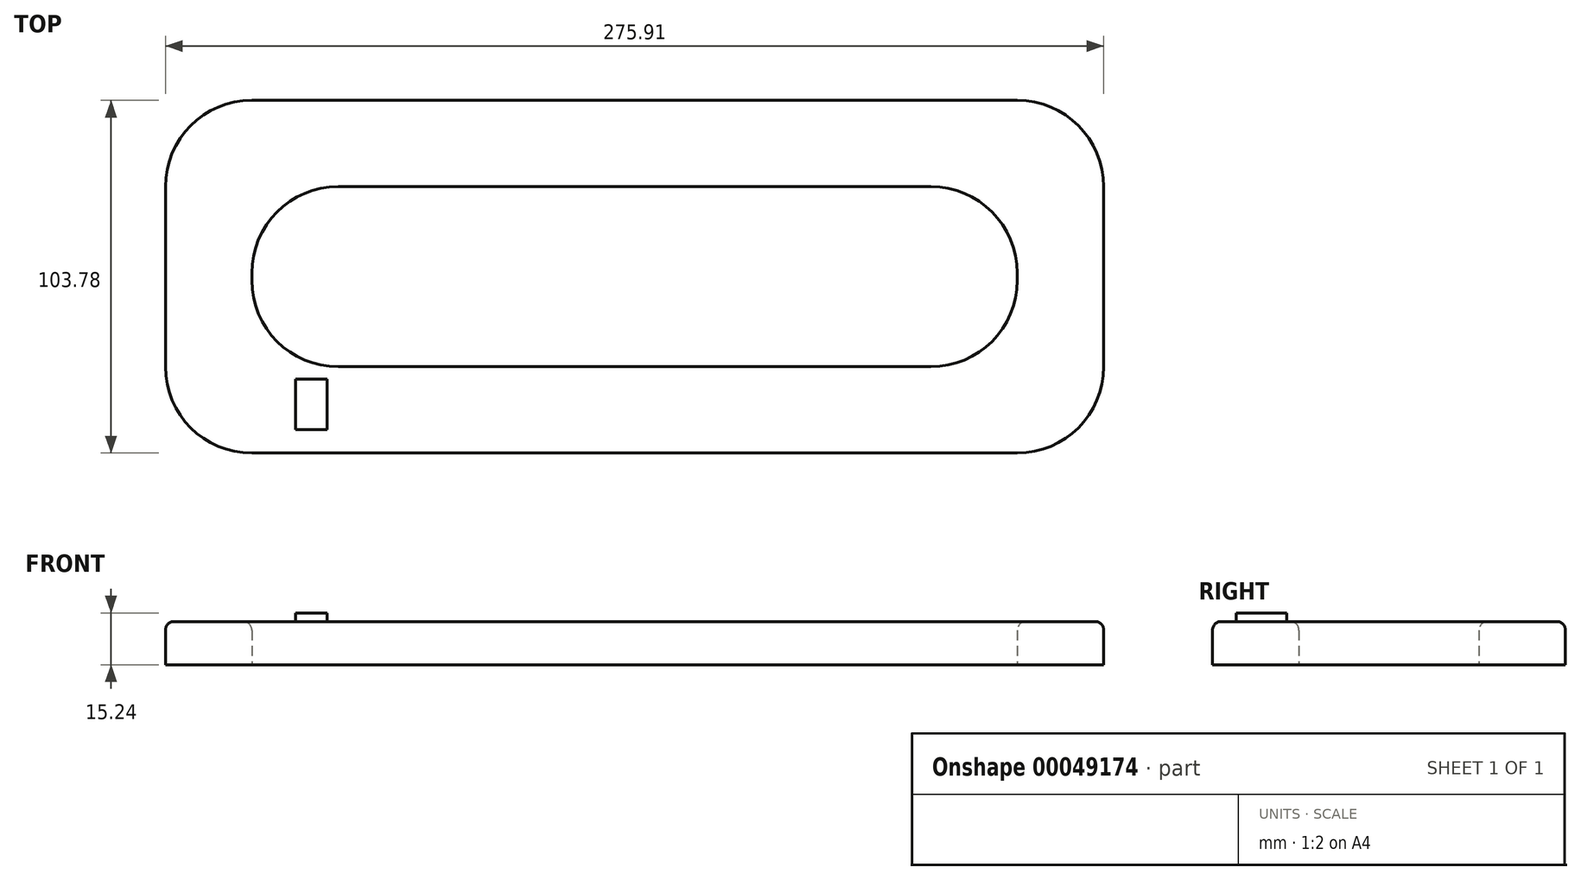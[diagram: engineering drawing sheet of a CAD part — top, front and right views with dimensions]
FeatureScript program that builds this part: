
annotation { "Feature Type Name" : "Feature", "Feature Type Description" : "" }
export const myFeature = defineFeature(function(context is Context, id is Id, definition is map)
    precondition{}
    {
        {
            var Q0;
            Q0=qCreatedBy(makeId("Top.planeOp"),FACE);
            var sketch = newSketch(context, id + "F0", { "sketchPlane" : qUnion([Q0])});
            skLineSegment(sketch, "E0.bottom", {"start": v(-102.88, -42.5) * mm, "end": v(71.43, -42.5) * mm});
            skLineSegment(sketch, "E0.top", {"start": v(-102.88, 10.48) * mm, "end": v(71.43, 10.48) * mm});
            skLineSegment(sketch, "E0.left", {"start": v(-128.28, -17.1) * mm, "end": v(-128.28, -14.92) * mm});
            skLineSegment(sketch, "E0.right", {"start": v(96.83, -17.1) * mm, "end": v(96.83, -14.92) * mm});
            skPoint(sketch, "E1.visualSharp", {"position": v(-128.28, 10.48) * mm});
            skArc(sketch, "E1.filletArc", {"start": v(-102.88, 10.48) * mm, "mid": v(-120.84, 3.04) * mm, "end": v(-128.28, -14.92) * mm});
            skPoint(sketch, "E2.visualSharp", {"position": v(-128.28, -42.5) * mm});
            skArc(sketch, "E2.filletArc", {"start": v(-128.28, -17.1) * mm, "mid": v(-120.84, -35.06) * mm, "end": v(-102.88, -42.5) * mm});
            skPoint(sketch, "E3.visualSharp", {"position": v(96.83, -42.5) * mm});
            skArc(sketch, "E3.filletArc", {"start": v(71.43, -42.5) * mm, "mid": v(89.4, -35.06) * mm, "end": v(96.83, -17.1) * mm});
            skPoint(sketch, "E4.visualSharp", {"position": v(96.83, 10.48) * mm});
            skArc(sketch, "E4.filletArc", {"start": v(96.83, -14.92) * mm, "mid": v(89.4, 3.04) * mm, "end": v(71.43, 10.48) * mm});
            skLineSegment(sketch, "E5.bottom", {"start": v(-128.28, 35.88) * mm, "end": v(96.83, 35.88) * mm});
            skLineSegment(sketch, "E5.top", {"start": v(-128.28, -67.9) * mm, "end": v(96.83, -67.9) * mm});
            skLineSegment(sketch, "E5.left", {"start": v(-153.68, 10.48) * mm, "end": v(-153.68, -42.5) * mm});
            skLineSegment(sketch, "E5.right", {"start": v(122.23, 10.48) * mm, "end": v(122.23, -42.5) * mm});
            skPoint(sketch, "E6.visualSharp", {"position": v(-153.68, -67.9) * mm});
            skArc(sketch, "E6.filletArc", {"start": v(-153.68, -42.5) * mm, "mid": v(-146.24, -60.46) * mm, "end": v(-128.28, -67.9) * mm});
            skPoint(sketch, "E7.visualSharp", {"position": v(-153.68, 35.88) * mm});
            skArc(sketch, "E7.filletArc", {"start": v(-128.28, 35.88) * mm, "mid": v(-146.24, 28.44) * mm, "end": v(-153.68, 10.48) * mm});
            skPoint(sketch, "E8.visualSharp", {"position": v(122.23, 35.88) * mm});
            skArc(sketch, "E8.filletArc", {"start": v(122.23, 10.48) * mm, "mid": v(114.8, 28.44) * mm, "end": v(96.83, 35.88) * mm});
            skPoint(sketch, "E9.visualSharp", {"position": v(122.23, -67.9) * mm});
            skArc(sketch, "E9.filletArc", {"start": v(96.83, -67.9) * mm, "mid": v(114.8, -60.46) * mm, "end": v(122.23, -42.5) * mm});
            skSolve(sketch);
        }
        {
            var Q0;
            Q0=makeQuery(id+"F0.imprint","IMPRINT",FACE,{"disambiguationData":[TD([[makeQuery(id+"F0.imprint","IMPRINT",EDGE,{"derivedFrom":sQuery(id+"F0.wireOp",EDGE,"E0.bottom")}),-1.0]])]});
            extrude(context, id + "F1", {"entities" : qUnion([Q0]), "depth" : 12.7 * mm});
        }
        {
            var Q0;
            Q0=makeQuery(id+"F1.opExtrude","CAP_FACE",FACE,{"disambiguationData":[OSD([sQuery(id+"F0.wireOp",EDGE,"E0.bottom"),sQuery(id+"F0.wireOp",EDGE,"E0.top"),sQuery(id+"F0.wireOp",EDGE,"E0.left"),sQuery(id+"F0.wireOp",EDGE,"E0.right"),sQuery(id+"F0.wireOp",EDGE,"E1.filletArc"),sQuery(id+"F0.wireOp",EDGE,"E2.filletArc"),sQuery(id+"F0.wireOp",EDGE,"E3.filletArc"),sQuery(id+"F0.wireOp",EDGE,"E4.filletArc"),sQuery(id+"F0.wireOp",EDGE,"E5.bottom"),sQuery(id+"F0.wireOp",EDGE,"E5.top"),sQuery(id+"F0.wireOp",EDGE,"E5.left"),sQuery(id+"F0.wireOp",EDGE,"E5.right"),sQuery(id+"F0.wireOp",EDGE,"E6.filletArc"),sQuery(id+"F0.wireOp",EDGE,"E7.filletArc"),sQuery(id+"F0.wireOp",EDGE,"E8.filletArc"),sQuery(id+"F0.wireOp",EDGE,"E9.filletArc")])],"isStart":false});
            fillet(context, id + "F2", {"entities" : qUnion([Q0]), "radius" : 2.54 * mm, "tangentPropagation" : true, "allowEdgeOverflow" : false});
        }
        {
            var Q0;
            Q0=makeQuery(id+"F1.opExtrude","CAP_FACE",FACE,{"disambiguationData":[OSD([sQuery(id+"F0.wireOp",EDGE,"E0.bottom"),sQuery(id+"F0.wireOp",EDGE,"E0.top"),sQuery(id+"F0.wireOp",EDGE,"E0.left"),sQuery(id+"F0.wireOp",EDGE,"E0.right"),sQuery(id+"F0.wireOp",EDGE,"E1.filletArc"),sQuery(id+"F0.wireOp",EDGE,"E2.filletArc"),sQuery(id+"F0.wireOp",EDGE,"E3.filletArc"),sQuery(id+"F0.wireOp",EDGE,"E4.filletArc"),sQuery(id+"F0.wireOp",EDGE,"E5.bottom"),sQuery(id+"F0.wireOp",EDGE,"E5.top"),sQuery(id+"F0.wireOp",EDGE,"E5.left"),sQuery(id+"F0.wireOp",EDGE,"E5.right"),sQuery(id+"F0.wireOp",EDGE,"E6.filletArc"),sQuery(id+"F0.wireOp",EDGE,"E7.filletArc"),sQuery(id+"F0.wireOp",EDGE,"E8.filletArc"),sQuery(id+"F0.wireOp",EDGE,"E9.filletArc")])],"isStart":false});
            var sketch = newSketch(context, id + "F3", { "sketchPlane" : qUnion([Q0])});
            skLineSegment(sketch, "E10.rect.bottom", {"start": v(-106.12, -60.92) * mm, "end": v(-115.4, -60.92) * mm});
            skLineSegment(sketch, "E10.rect.top", {"start": v(-106.12, -46.08) * mm, "end": v(-115.4, -46.08) * mm});
            skLineSegment(sketch, "E10.rect.left", {"start": v(-106.12, -60.92) * mm, "end": v(-106.12, -46.08) * mm});
            skLineSegment(sketch, "E10.rect.right", {"start": v(-115.4, -60.92) * mm, "end": v(-115.4, -46.08) * mm});
            skPoint(sketch, "E10.rect.middle", {"position": v(-110.76, -53.5) * mm});
            skLineSegment(sketch, "E11.MirrorCS", {"start": v(-96.83, -60.92) * mm, "end": v(-96.83, -46.08) * mm});
            skLineSegment(sketch, "E12.MirrorCS", {"start": v(-106.12, -60.92) * mm, "end": v(-96.83, -60.92) * mm});
            skLineSegment(sketch, "E13.MirrorCS", {"start": v(-106.12, -46.08) * mm, "end": v(-96.83, -46.08) * mm});
            skSolve(sketch);
        }
        {
            var Q0;
            Q0=makeQuery(id+"F3.imprint","IMPRINT",FACE,{"disambiguationData":[TD([[makeQuery(id+"F3.imprint","IMPRINT",EDGE,{"derivedFrom":sQuery(id+"F3.wireOp",EDGE,"E10.rect.left")}),1.0]])]});
            extrude(context, id + "F4", {"entities" : qUnion([Q0]), "operationType" : NewBodyOperationType.ADD, "depth" : 2.54 * mm});
        }
    });
